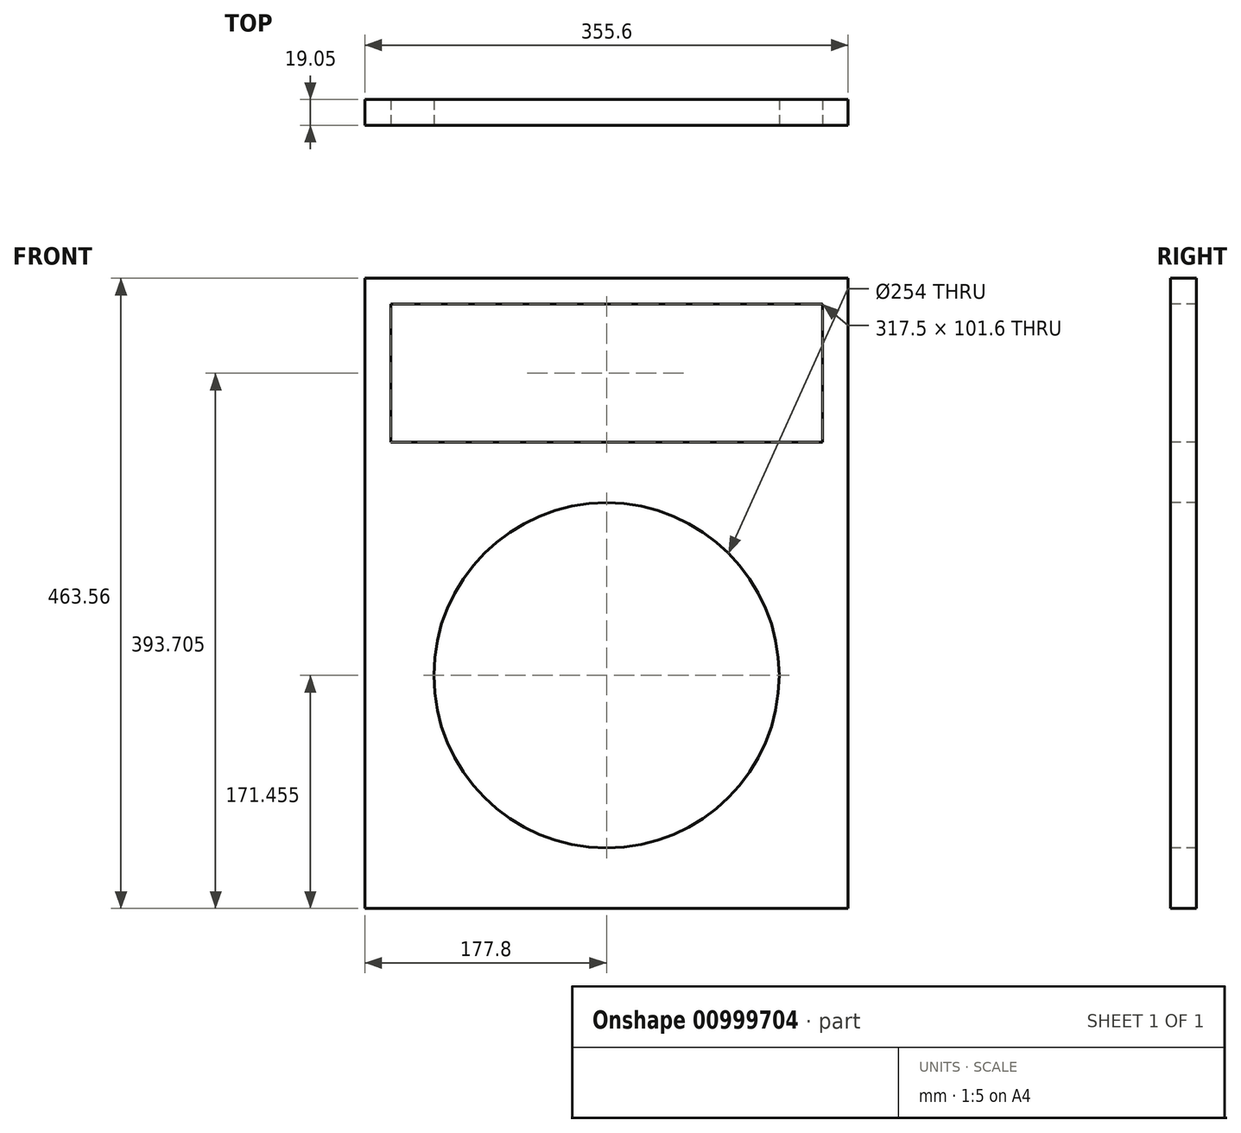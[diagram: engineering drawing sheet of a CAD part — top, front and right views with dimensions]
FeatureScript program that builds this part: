
annotation { "Feature Type Name" : "Feature", "Feature Type Description" : "" }
export const myFeature = defineFeature(function(context is Context, id is Id, definition is map)
    precondition{}
    {
        {
            var Q0;
            Q0=qCreatedBy(makeId("Front.planeOp"),FACE);
            var sketch = newSketch(context, id + "F0", { "sketchPlane" : qUnion([Q0])});
            skLineSegment(sketch, "E0.bottom", {"start": v(-177.8, -231.77) * mm, "end": v(177.8, -231.77) * mm});
            skLineSegment(sketch, "E0.top", {"start": v(-177.8, 231.78) * mm, "end": v(177.8, 231.78) * mm});
            skLineSegment(sketch, "E0.left", {"start": v(-177.8, -231.77) * mm, "end": v(-177.8, 231.78) * mm});
            skLineSegment(sketch, "E0.right", {"start": v(177.8, -231.77) * mm, "end": v(177.8, 231.78) * mm});
            skPoint(sketch, "E0.middle", {"position": v(0, 0) * mm});
            skSolve(sketch);
        }
        {
            var Q0;
            Q0=makeQuery(id+"F0.imprint","IMPRINT",FACE,{"disambiguationData":[TD([[makeQuery(id+"F0.imprint","IMPRINT",EDGE,{"derivedFrom":sQuery(id+"F0.wireOp",EDGE,"E0.bottom")}),1.0]])]});
            extrude(context, id + "F1", {"entities" : qUnion([Q0]), "depth" : 19.05 * mm, "offsetDistance" : 25.4 * mm});
        }
        {
            var Q0;
            Q0=makeQuery(id+"F1.opExtrude","CAP_FACE",FACE,{"disambiguationData":[OSD([sQuery(id+"F0.wireOp",EDGE,"E0.bottom"),sQuery(id+"F0.wireOp",EDGE,"E0.top"),sQuery(id+"F0.wireOp",EDGE,"E0.left"),sQuery(id+"F0.wireOp",EDGE,"E0.right")])],"isStart":false});
            var sketch = newSketch(context, id + "F2", { "sketchPlane" : qUnion([Q0])});
            skLineSegment(sketch, "E1.bottom", {"start": v(-158.75, 212.72) * mm, "end": v(158.75, 212.72) * mm});
            skLineSegment(sketch, "E1.top", {"start": v(-158.75, 111.12) * mm, "end": v(158.75, 111.12) * mm});
            skLineSegment(sketch, "E1.left", {"start": v(-158.75, 212.72) * mm, "end": v(-158.75, 111.12) * mm});
            skLineSegment(sketch, "E1.right", {"start": v(158.75, 212.72) * mm, "end": v(158.75, 111.12) * mm});
            skSolve(sketch);
        }
        {
            var Q0;
            Q0 = qSketchRegion(id + "F2", true);
            extrude(context, id + "F3", {"entities" : qUnion([Q0]), "operationType" : NewBodyOperationType.REMOVE, "endBound" : BoundingType.THROUGH_ALL, "oppositeDirection" : true, "depth" : 25.4 * mm, "offsetDistance" : 25.4 * mm});
        }
        {
            var Q0;
            Q0=makeQuery(id+"F2.imprint","IMPRINT",FACE,{"disambiguationData":[TD([[makeQuery(id+"F2.imprint","IMPRINT",EDGE,{"derivedFrom":sQuery(id+"F2.wireOp",EDGE,"E1.bottom")}),1.0]])]});
            var sketch = newSketch(context, id + "F4", { "sketchPlane" : qUnion([Q0])});
            skPoint(sketch, "E2", {"position": v(0, -60.33) * mm});
            skCircle(sketch, "E3", {"center": v(0, -60.33) * mm, "radius": 127 * mm});
            skSolve(sketch);
        }
        {
            var Q0;
            Q0 = qSketchRegion(id + "F4", true);
            extrude(context, id + "F5", {"entities" : qUnion([Q0]), "operationType" : NewBodyOperationType.REMOVE, "endBound" : BoundingType.THROUGH_ALL, "oppositeDirection" : true, "depth" : 25.4 * mm, "offsetDistance" : 25.4 * mm});
        }
    });
